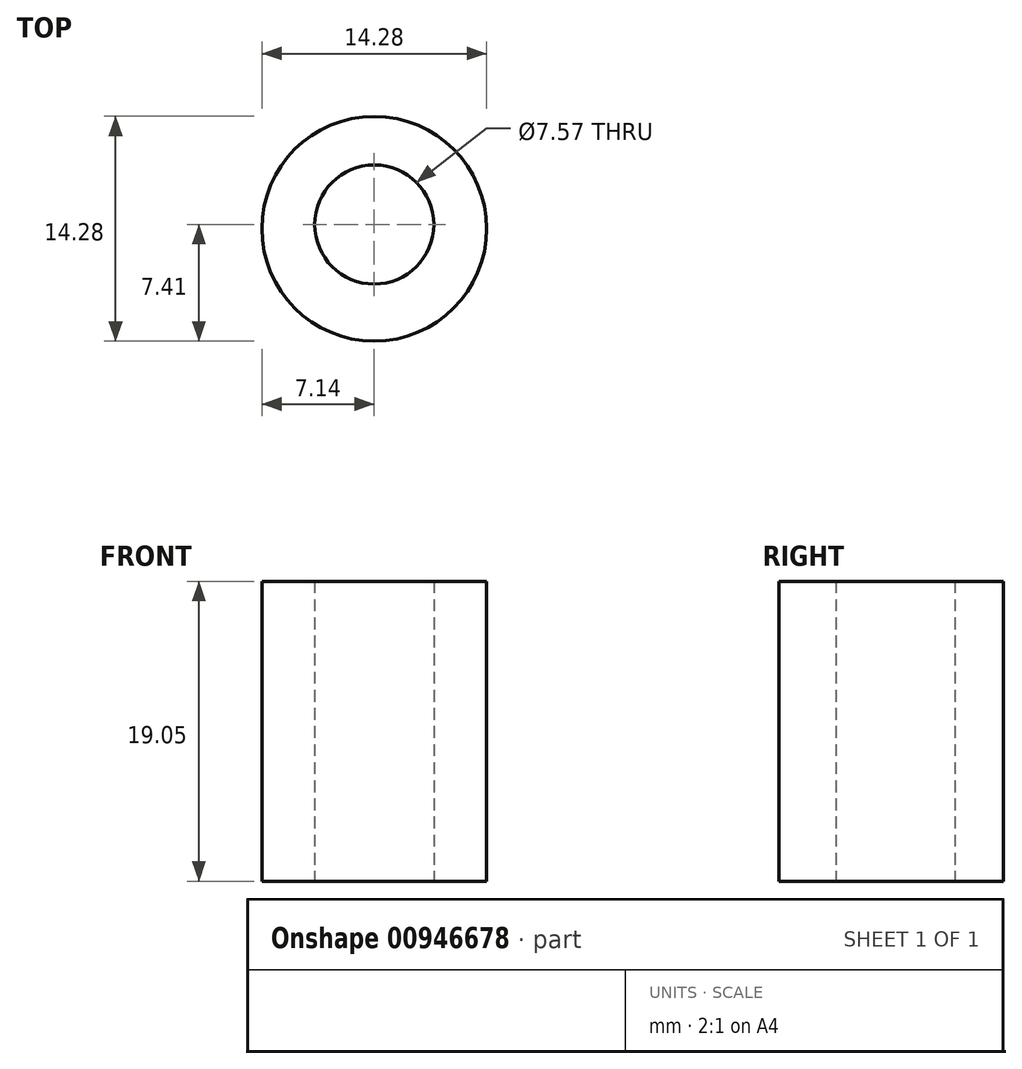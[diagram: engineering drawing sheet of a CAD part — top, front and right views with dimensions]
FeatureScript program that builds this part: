
annotation { "Feature Type Name" : "Feature", "Feature Type Description" : "" }
export const myFeature = defineFeature(function(context is Context, id is Id, definition is map)
    precondition{}
    {
        {
            var Q0;
            Q0=qCreatedBy(makeId("Top.planeOp"),FACE);
            var sketch = newSketch(context, id + "F0", { "sketchPlane" : qUnion([Q0])});
            skCircle(sketch, "E0", {"center": v(0, 0) * mm, "radius": 7.14 * mm});
            skCircle(sketch, "E1", {"center": v(0, 0.27) * mm, "radius": 3.78 * mm});
            skSolve(sketch);
        }
        {
            var Q0;
            Q0 = qSketchRegion(id + "F0", true);
            extrude(context, id + "F1", {"entities" : qUnion([Q0]), "depth" : 19.05 * mm, "offsetDistance" : 25.4 * mm});
        }
    });
